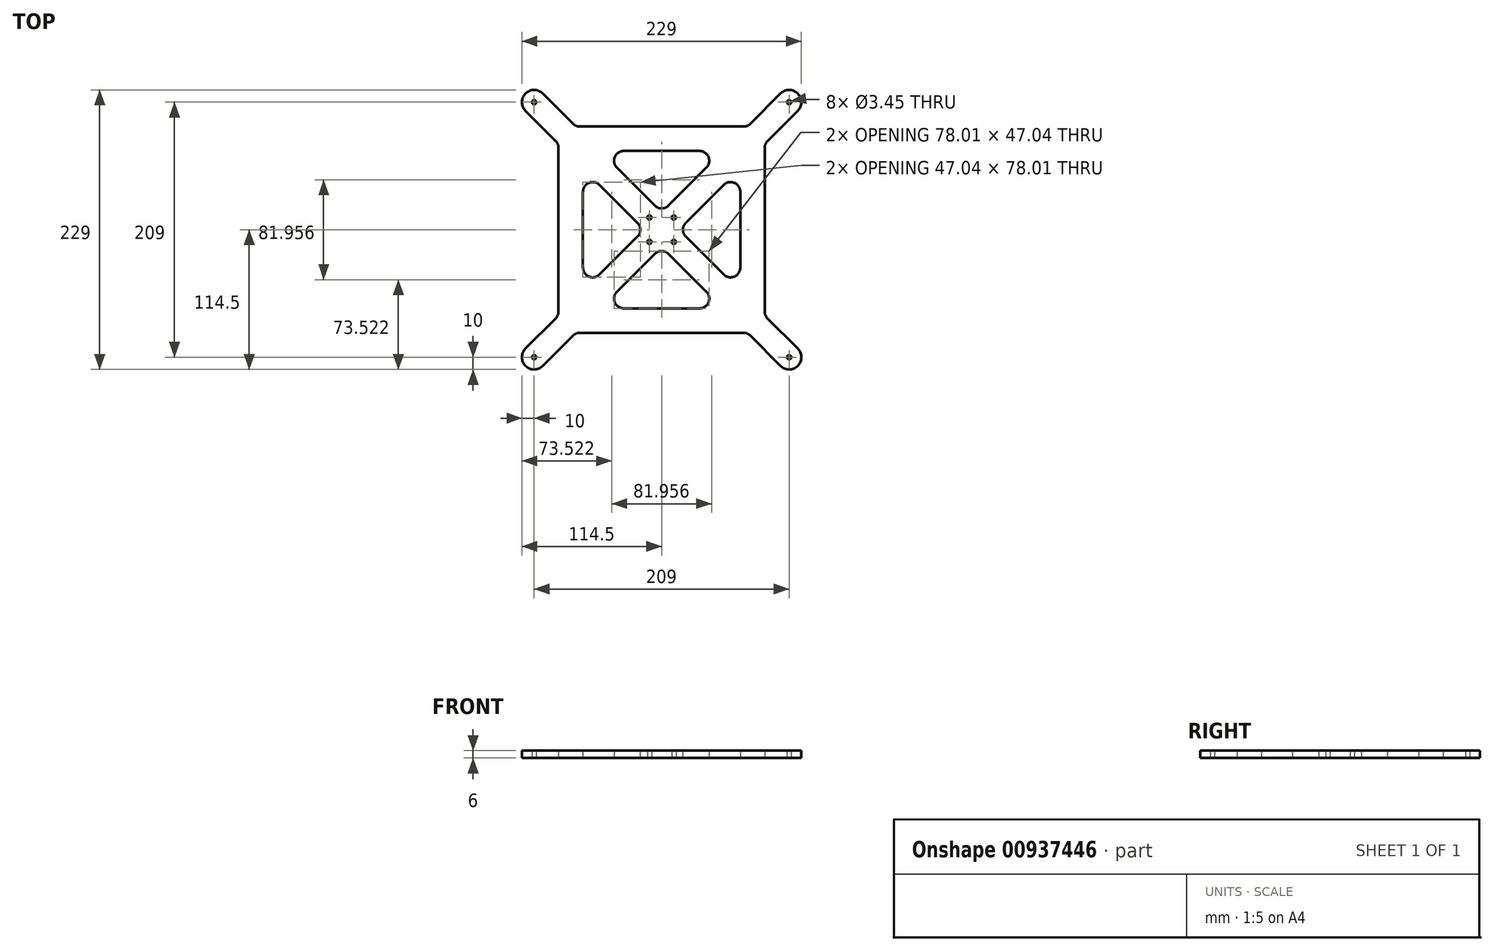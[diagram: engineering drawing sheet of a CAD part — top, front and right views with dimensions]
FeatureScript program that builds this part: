
annotation { "Feature Type Name" : "Feature", "Feature Type Description" : "" }
export const myFeature = defineFeature(function(context is Context, id is Id, definition is map)
    precondition{}
    {
        {
            var Q0;
            Q0=qCreatedBy(makeId("Top.planeOp"),FACE);
            var sketch = newSketch(context, id + "F0", { "sketchPlane" : qUnion([Q0])});
            skLineSegment(sketch, "E0.bottom", {"start": v(0, 0) * mm, "end": v(209, 0) * mm, "construction": true});
            skLineSegment(sketch, "E0.top", {"start": v(0, 209) * mm, "end": v(209, 209) * mm, "construction": true});
            skLineSegment(sketch, "E0.left", {"start": v(0, 0) * mm, "end": v(0, 209) * mm, "construction": true});
            skLineSegment(sketch, "E0.right", {"start": v(209, 0) * mm, "end": v(209, 209) * mm, "construction": true});
            skCircle(sketch, "E1", {"center": v(0, 209) * mm, "radius": 1.72 * mm});
            skCircle(sketch, "E2", {"center": v(209, 209) * mm, "radius": 1.72 * mm});
            skCircle(sketch, "E3", {"center": v(209, 0) * mm, "radius": 1.72 * mm});
            skCircle(sketch, "E4", {"center": v(0, 0) * mm, "radius": 1.72 * mm});
            skLineSegment(sketch, "E5", {"start": v(104.5, 0) * mm, "end": v(104.5, 104.5) * mm, "construction": true});
            skLineSegment(sketch, "E6", {"start": v(104.5, 104.5) * mm, "end": v(209, 104.5) * mm, "construction": true});
            skLineSegment(sketch, "E7.bottom", {"start": v(94.5, 114.5) * mm, "end": v(114.5, 114.5) * mm, "construction": true});
            skLineSegment(sketch, "E7.top", {"start": v(94.5, 94.5) * mm, "end": v(114.5, 94.5) * mm, "construction": true});
            skLineSegment(sketch, "E7.left", {"start": v(94.5, 114.5) * mm, "end": v(94.5, 94.5) * mm, "construction": true});
            skLineSegment(sketch, "E7.right", {"start": v(114.5, 114.5) * mm, "end": v(114.5, 94.5) * mm, "construction": true});
            skLineSegment(sketch, "E8", {"start": v(104.5, 104.5) * mm, "end": v(104.5, 114.5) * mm, "construction": true});
            skLineSegment(sketch, "E9", {"start": v(104.5, 104.5) * mm, "end": v(94.5, 104.5) * mm, "construction": true});
            skCircle(sketch, "E10", {"center": v(94.5, 114.5) * mm, "radius": 1.73 * mm});
            skCircle(sketch, "E11", {"center": v(114.5, 114.5) * mm, "radius": 1.73 * mm});
            skCircle(sketch, "E12", {"center": v(114.5, 94.5) * mm, "radius": 1.73 * mm});
            skCircle(sketch, "E13", {"center": v(94.5, 94.5) * mm, "radius": 1.73 * mm});
            skCircle(sketch, "E14", {"center": v(0, 209) * mm, "radius": 10 * mm});
            skCircle(sketch, "E15", {"center": v(209, 209) * mm, "radius": 10 * mm});
            skCircle(sketch, "E16", {"center": v(209, 0) * mm, "radius": 10 * mm});
            skCircle(sketch, "E17", {"center": v(0, 0) * mm, "radius": 10 * mm});
            skLineSegment(sketch, "E18", {"start": v(7.07, 216.07) * mm, "end": v(216.07, 7.07) * mm});
            skLineSegment(sketch, "E19", {"start": v(-7.07, 201.93) * mm, "end": v(201.93, -7.07) * mm});
            skLineSegment(sketch, "E20", {"start": v(216.07, 201.93) * mm, "end": v(7.07, -7.07) * mm});
            skLineSegment(sketch, "E21", {"start": v(201.93, 216.07) * mm, "end": v(-7.07, 7.07) * mm});
            skLineSegment(sketch, "E22", {"start": v(34.14, 189) * mm, "end": v(174.86, 189) * mm});
            skLineSegment(sketch, "E23", {"start": v(154.86, 169) * mm, "end": v(54.14, 169) * mm});
            skLineSegment(sketch, "E24", {"start": v(169, 154.86) * mm, "end": v(169, 54.14) * mm});
            skLineSegment(sketch, "E25", {"start": v(189, 174.86) * mm, "end": v(189, 34.14) * mm});
            skLineSegment(sketch, "E26", {"start": v(154.86, 40) * mm, "end": v(54.14, 40) * mm});
            skLineSegment(sketch, "E27", {"start": v(34.14, 20) * mm, "end": v(174.86, 20) * mm});
            skLineSegment(sketch, "E28", {"start": v(40, 54.14) * mm, "end": v(40, 154.86) * mm});
            skLineSegment(sketch, "E29", {"start": v(20, 174.86) * mm, "end": v(20, 34.14) * mm});
            skSolve(sketch);
        }
        {
            var Q0;
            Q0 = qSketchRegion(id + "F0", true);
            var Q1;
            {var subQ0=sQuery(id+"F0.wireOp",EDGE,"E21");var subQ1=sQuery(id+"F0.wireOp",EDGE,"E18");var subQ2=makeQuery(id+"F0.imprint","INTERSECT",VERTEX,{"derivedFrom":[subQ1,subQ0]});Q1=makeQuery(id+"F0.imprint","IMPRINT",FACE,{"disambiguationData":[TD([[makeQuery(id+"F0.imprint","IMPRINT",EDGE,{"disambiguationData":[TD([[subQ2,-1.0]])],"derivedFrom":subQ1}),-1.0]])]});}
            extrude(context, id + "F1", {"entities" : qUnion([Q0, Q1]), "depth" : 6 * mm, "offsetDistance" : 25 * mm});
        }
        {
            var Q0;
            Q0=makeQuery(id+"F1.opExtrude","SWEPT_EDGE",EDGE,{"disambiguationData":[OSD([sQuery(id+"F0.wireOp",EDGE,"E19"),sQuery(id+"F0.wireOp",EDGE,"E29")])]});
            var Q1;
            Q1=makeQuery(id+"F1.opExtrude","SWEPT_EDGE",EDGE,{"disambiguationData":[OSD([sQuery(id+"F0.wireOp",EDGE,"E21"),sQuery(id+"F0.wireOp",EDGE,"E29")])]});
            var Q2;
            Q2=makeQuery(id+"F1.opExtrude","SWEPT_EDGE",EDGE,{"disambiguationData":[OSD([sQuery(id+"F0.wireOp",EDGE,"E20"),sQuery(id+"F0.wireOp",EDGE,"E27")])]});
            var Q3;
            Q3=makeQuery(id+"F1.opExtrude","SWEPT_EDGE",EDGE,{"disambiguationData":[OSD([sQuery(id+"F0.wireOp",EDGE,"E19"),sQuery(id+"F0.wireOp",EDGE,"E27")])]});
            var Q4;
            Q4=makeQuery(id+"F1.opExtrude","SWEPT_EDGE",EDGE,{"disambiguationData":[OSD([sQuery(id+"F0.wireOp",EDGE,"E20"),sQuery(id+"F0.wireOp",EDGE,"E25")])]});
            var Q5;
            Q5=makeQuery(id+"F1.opExtrude","SWEPT_EDGE",EDGE,{"disambiguationData":[OSD([sQuery(id+"F0.wireOp",EDGE,"E18"),sQuery(id+"F0.wireOp",EDGE,"E25")])]});
            var Q6;
            Q6=makeQuery(id+"F1.opExtrude","SWEPT_EDGE",EDGE,{"disambiguationData":[OSD([sQuery(id+"F0.wireOp",EDGE,"E21"),sQuery(id+"F0.wireOp",EDGE,"E22")])]});
            var Q7;
            Q7=makeQuery(id+"F1.opExtrude","SWEPT_EDGE",EDGE,{"disambiguationData":[OSD([sQuery(id+"F0.wireOp",EDGE,"E18"),sQuery(id+"F0.wireOp",EDGE,"E22")])]});
            var Q8;
            Q8=makeQuery(id+"F1.opExtrude","SWEPT_EDGE",EDGE,{"disambiguationData":[OSD([sQuery(id+"F0.wireOp",EDGE,"E18"),sQuery(id+"F0.wireOp",EDGE,"E21")])]});
            var Q9;
            Q9=makeQuery(id+"F1.opExtrude","SWEPT_EDGE",EDGE,{"disambiguationData":[OSD([sQuery(id+"F0.wireOp",EDGE,"E21"),sQuery(id+"F0.wireOp",EDGE,"E23")])]});
            var Q10;
            Q10=makeQuery(id+"F1.opExtrude","SWEPT_EDGE",EDGE,{"disambiguationData":[OSD([sQuery(id+"F0.wireOp",EDGE,"E19"),sQuery(id+"F0.wireOp",EDGE,"E21")])]});
            var Q11;
            Q11=makeQuery(id+"F1.opExtrude","SWEPT_EDGE",EDGE,{"disambiguationData":[OSD([sQuery(id+"F0.wireOp",EDGE,"E19"),sQuery(id+"F0.wireOp",EDGE,"E20")])]});
            var Q12;
            Q12=makeQuery(id+"F1.opExtrude","SWEPT_EDGE",EDGE,{"disambiguationData":[OSD([sQuery(id+"F0.wireOp",EDGE,"E20"),sQuery(id+"F0.wireOp",EDGE,"E24")])]});
            var Q13;
            Q13=makeQuery(id+"F1.opExtrude","SWEPT_EDGE",EDGE,{"disambiguationData":[OSD([sQuery(id+"F0.wireOp",EDGE,"E18"),sQuery(id+"F0.wireOp",EDGE,"E23")])]});
            var Q14;
            Q14=makeQuery(id+"F1.opExtrude","SWEPT_EDGE",EDGE,{"disambiguationData":[OSD([sQuery(id+"F0.wireOp",EDGE,"E18"),sQuery(id+"F0.wireOp",EDGE,"E20")])]});
            var Q15;
            Q15=makeQuery(id+"F1.opExtrude","SWEPT_EDGE",EDGE,{"disambiguationData":[OSD([sQuery(id+"F0.wireOp",EDGE,"E21"),sQuery(id+"F0.wireOp",EDGE,"E28")])]});
            var Q16;
            Q16=makeQuery(id+"F1.opExtrude","SWEPT_EDGE",EDGE,{"disambiguationData":[OSD([sQuery(id+"F0.wireOp",EDGE,"E20"),sQuery(id+"F0.wireOp",EDGE,"E26")])]});
            var Q17;
            Q17=makeQuery(id+"F1.opExtrude","SWEPT_EDGE",EDGE,{"disambiguationData":[OSD([sQuery(id+"F0.wireOp",EDGE,"E19"),sQuery(id+"F0.wireOp",EDGE,"E26")])]});
            var Q18;
            Q18=makeQuery(id+"F1.opExtrude","SWEPT_EDGE",EDGE,{"disambiguationData":[OSD([sQuery(id+"F0.wireOp",EDGE,"E18"),sQuery(id+"F0.wireOp",EDGE,"E24")])]});
            var Q19;
            Q19=makeQuery(id+"F1.opExtrude","SWEPT_EDGE",EDGE,{"disambiguationData":[OSD([sQuery(id+"F0.wireOp",EDGE,"E19"),sQuery(id+"F0.wireOp",EDGE,"E28")])]});
            fillet(context, id + "F2", {"entities" : qUnion([Q0, Q1, Q2, Q3, Q4, Q5, Q6, Q7, Q8, Q9, Q10, Q11, Q12, Q13, Q14, Q15, Q16, Q17, Q18, Q19]), "radius" : 8 * mm, "tangentPropagation" : true, "allowEdgeOverflow" : false});
        }
    });
